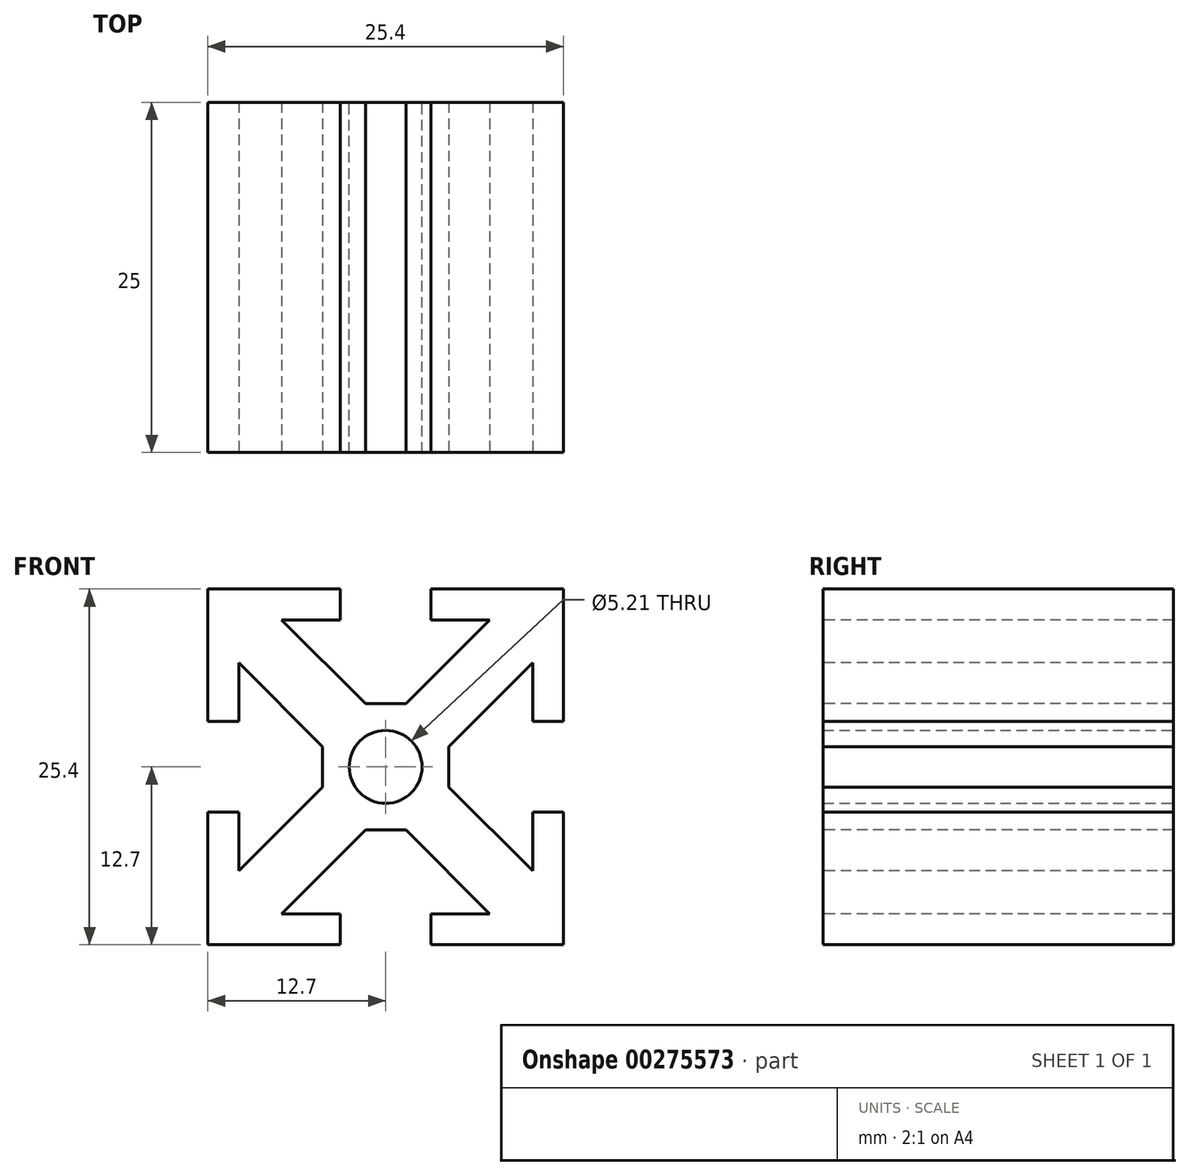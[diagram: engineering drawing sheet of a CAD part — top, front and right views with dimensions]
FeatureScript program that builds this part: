
annotation { "Feature Type Name" : "Feature", "Feature Type Description" : "" }
export const myFeature = defineFeature(function(context is Context, id is Id, definition is map)
    precondition{}
    {
        {
            var Q0;
            Q0=qCreatedBy(makeId("Front.planeOp"),FACE);
            var sketch = newSketch(context, id + "F0", { "sketchPlane" : qUnion([Q0])});
            skCircle(sketch, "E0", {"center": v(0, 0) * mm, "radius": 2.6 * mm});
            skLineSegment(sketch, "E1.bottom", {"start": v(12.7, -12.7) * mm, "end": v(-12.7, -12.7) * mm});
            skLineSegment(sketch, "E1.top", {"start": v(12.7, 12.7) * mm, "end": v(-12.7, 12.7) * mm});
            skLineSegment(sketch, "E1.left", {"start": v(12.7, -12.7) * mm, "end": v(12.7, 12.7) * mm});
            skLineSegment(sketch, "E1.right", {"start": v(-12.7, -12.7) * mm, "end": v(-12.7, 12.7) * mm});
            skSolve(sketch);
        }
        {
            var Q0;
            Q0 = qSketchRegion(id + "F0", true);
            extrude(context, id + "F1", {"entities" : qUnion([Q0]), "endBound" : BoundingType.SYMMETRIC, "depth" : 25 * mm});
        }
        {
            var Q0;
            Q0=makeQuery(id+"F1.opExtrude","CAP_FACE",FACE,{"disambiguationData":[OSD([sQuery(id+"F0.wireOp",EDGE,"E0"),sQuery(id+"F0.wireOp",EDGE,"E1.bottom"),sQuery(id+"F0.wireOp",EDGE,"E1.top"),sQuery(id+"F0.wireOp",EDGE,"E1.left"),sQuery(id+"F0.wireOp",EDGE,"E1.right")])],"isStart":false});
            var sketch = newSketch(context, id + "F2", { "sketchPlane" : qUnion([Q0])});
            skLineSegment(sketch, "E2", {"start": v(0, 0) * mm, "end": v(0, 12.7) * mm, "construction": true});
            skLineSegment(sketch, "E3", {"start": v(-3.24, 12.7) * mm, "end": v(-3.24, 10.5) * mm});
            skLineSegment(sketch, "E4", {"start": v(-3.24, 10.5) * mm, "end": v(-7.43, 10.5) * mm});
            skLineSegment(sketch, "E5", {"start": v(-7.43, 10.5) * mm, "end": v(-1.45, 4.5) * mm});
            skLineSegment(sketch, "E6.MirrorCS", {"start": v(7.43, 10.5) * mm, "end": v(1.45, 4.5) * mm});
            skLineSegment(sketch, "E7.MirrorCS", {"start": v(3.24, 12.7) * mm, "end": v(3.24, 10.5) * mm});
            skLineSegment(sketch, "E8.MirrorCS", {"start": v(3.24, 10.5) * mm, "end": v(7.43, 10.5) * mm});
            skLineSegment(sketch, "E9", {"start": v(-3.24, 12.7) * mm, "end": v(3.24, 12.7) * mm});
            skLineSegment(sketch, "E10", {"start": v(-1.45, 4.5) * mm, "end": v(1.45, 4.5) * mm});
            skLineSegment(sketch, "E11.1.0", {"start": v(-12.7, -3.24) * mm, "end": v(-12.7, 3.24) * mm});
            skLineSegment(sketch, "E11.1.1", {"start": v(-12.7, -3.24) * mm, "end": v(-10.5, -3.24) * mm});
            skLineSegment(sketch, "E11.1.2", {"start": v(-10.5, -3.24) * mm, "end": v(-10.5, -7.43) * mm});
            skLineSegment(sketch, "E11.1.3", {"start": v(-10.5, -7.43) * mm, "end": v(-4.5, -1.45) * mm});
            skLineSegment(sketch, "E11.1.4", {"start": v(-4.5, -1.45) * mm, "end": v(-4.5, 1.45) * mm});
            skLineSegment(sketch, "E11.1.5", {"start": v(-10.5, 7.43) * mm, "end": v(-4.5, 1.45) * mm});
            skLineSegment(sketch, "E11.1.6", {"start": v(-10.5, 3.24) * mm, "end": v(-10.5, 7.43) * mm});
            skLineSegment(sketch, "E11.1.7", {"start": v(-12.7, 3.24) * mm, "end": v(-10.5, 3.24) * mm});
            skLineSegment(sketch, "E11.2.0", {"start": v(3.24, -12.7) * mm, "end": v(-3.24, -12.7) * mm});
            skLineSegment(sketch, "E11.2.1", {"start": v(3.24, -12.7) * mm, "end": v(3.24, -10.5) * mm});
            skLineSegment(sketch, "E11.2.2", {"start": v(3.24, -10.5) * mm, "end": v(7.43, -10.5) * mm});
            skLineSegment(sketch, "E11.2.3", {"start": v(7.43, -10.5) * mm, "end": v(1.45, -4.5) * mm});
            skLineSegment(sketch, "E11.2.4", {"start": v(1.45, -4.5) * mm, "end": v(-1.45, -4.5) * mm});
            skLineSegment(sketch, "E11.2.5", {"start": v(-7.43, -10.5) * mm, "end": v(-1.45, -4.5) * mm});
            skLineSegment(sketch, "E11.2.6", {"start": v(-3.24, -10.5) * mm, "end": v(-7.43, -10.5) * mm});
            skLineSegment(sketch, "E11.2.7", {"start": v(-3.24, -12.7) * mm, "end": v(-3.24, -10.5) * mm});
            skPoint(sketch, "E11.center", {"position": v(0, 0) * mm});
            skLineSegment(sketch, "E12.3.3.0", {"start": v(12.7, 3.24) * mm, "end": v(10.5, 3.24) * mm});
            skLineSegment(sketch, "E12.6.3.0", {"start": v(10.5, 3.24) * mm, "end": v(10.5, 7.43) * mm});
            skLineSegment(sketch, "E12.9.3.0", {"start": v(10.5, 7.43) * mm, "end": v(4.5, 1.45) * mm});
            skLineSegment(sketch, "E12.11.3.0", {"start": v(12.7, 3.24) * mm, "end": v(12.7, -3.24) * mm});
            skLineSegment(sketch, "E12.12.3.0", {"start": v(4.5, 1.45) * mm, "end": v(4.5, -1.45) * mm});
            skLineSegment(sketch, "E12.15.3.0", {"start": v(10.5, -7.43) * mm, "end": v(4.5, -1.45) * mm});
            skLineSegment(sketch, "E12.18.3.0", {"start": v(10.5, -3.24) * mm, "end": v(10.5, -7.43) * mm});
            skLineSegment(sketch, "E12.21.3.0", {"start": v(12.7, -3.24) * mm, "end": v(10.5, -3.24) * mm});
            skSolve(sketch);
        }
        {
            var Q0;
            Q0 = qSketchRegion(id + "F2", true);
            extrude(context, id + "F3", {"entities" : qUnion([Q0]), "operationType" : NewBodyOperationType.REMOVE, "endBound" : BoundingType.THROUGH_ALL, "oppositeDirection" : true, "depth" : 25 * mm});
        }
    });
